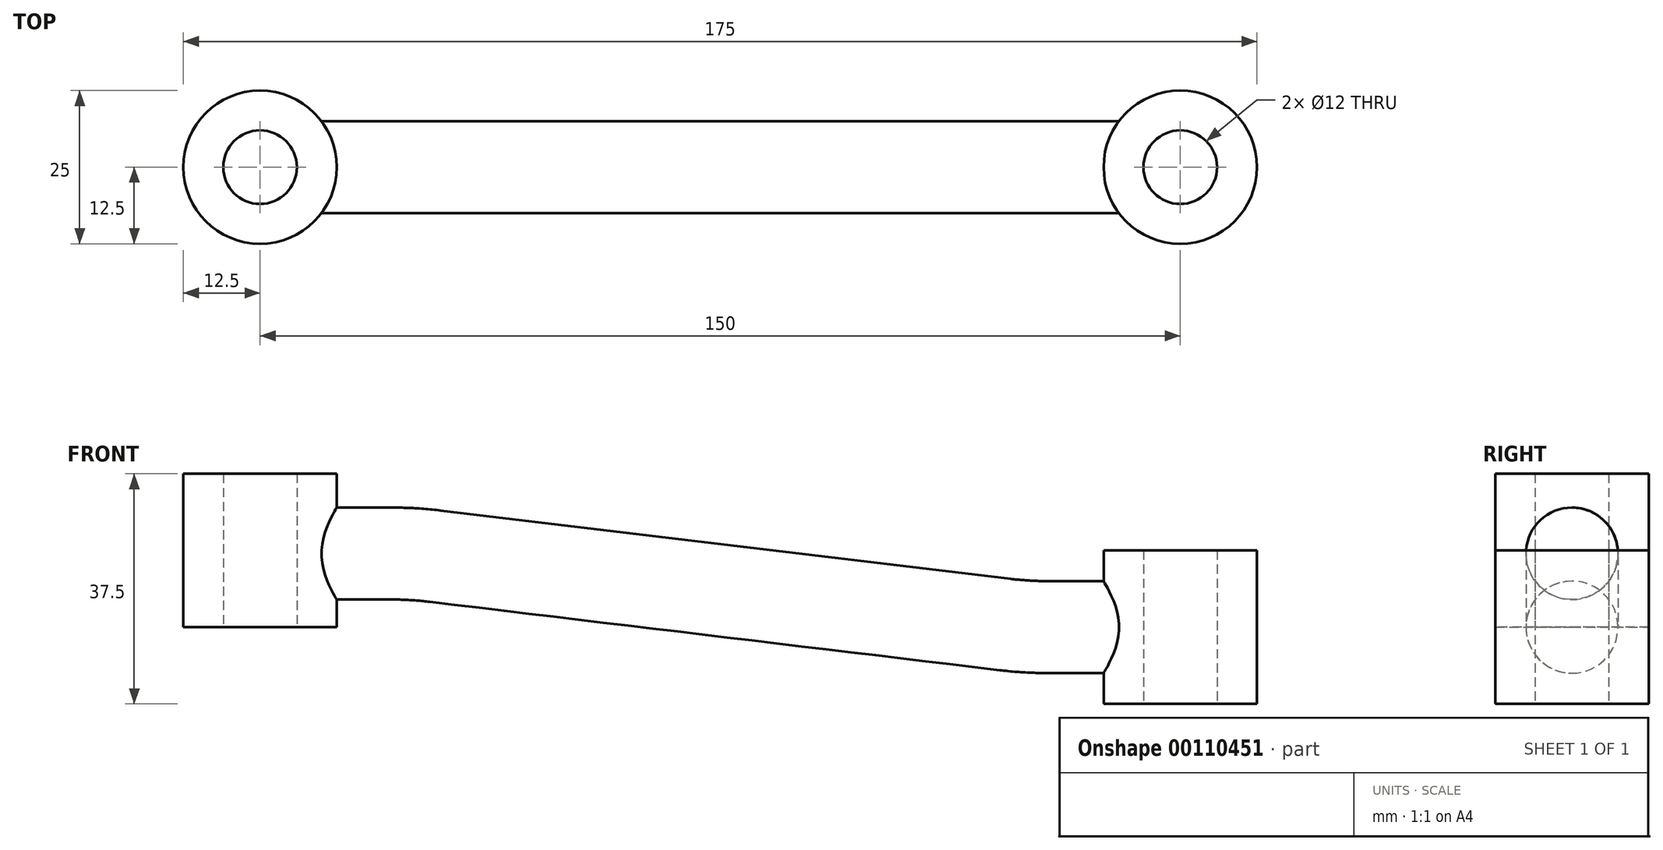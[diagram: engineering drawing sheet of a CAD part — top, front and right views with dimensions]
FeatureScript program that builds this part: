
annotation { "Feature Type Name" : "Feature", "Feature Type Description" : "" }
export const myFeature = defineFeature(function(context is Context, id is Id, definition is map)
    precondition{}
    {
        {
            var Q0;
            Q0=qCreatedBy(makeId("Top.planeOp"),FACE);
            var sketch = newSketch(context, id + "F0", { "sketchPlane" : qUnion([Q0])});
            skCircle(sketch, "E0", {"center": v(0, 0) * mm, "radius": 12.5 * mm});
            skCircle(sketch, "E1", {"center": v(0, 0) * mm, "radius": 6 * mm});
            skSolve(sketch);
        }
        {
            var Q0;
            Q0 = qSketchRegion(id + "F0", true);
            extrude(context, id + "F1", {"entities" : qUnion([Q0]), "depth" : 25 * mm});
        }
        {
            var Q0;
            Q0=qCreatedBy(makeId("Front.planeOp"),FACE);
            var sketch = newSketch(context, id + "F2", { "sketchPlane" : qUnion([Q0])});
            skLineSegment(sketch, "E2", {"start": v(0, 0) * mm, "end": v(0, 12) * mm, "construction": true});
            skLineSegment(sketch, "E3", {"start": v(0, 12) * mm, "end": v(21.41, 12) * mm});
            skLineSegment(sketch, "E4", {"start": v(28.56, 11.57) * mm, "end": v(121.44, 0.43) * mm});
            skLineSegment(sketch, "E5", {"start": v(128.59, 0) * mm, "end": v(150, 0) * mm});
            skPoint(sketch, "E6.visualSharp", {"position": v(25, 12) * mm});
            skArc(sketch, "E6.filletArc", {"start": v(28.56, 11.57) * mm, "mid": v(25, 11.9) * mm, "end": v(21.41, 12) * mm});
            skPoint(sketch, "E7.visualSharp", {"position": v(125, 0) * mm});
            skArc(sketch, "E7.filletArc", {"start": v(121.44, 0.43) * mm, "mid": v(125, 0.1) * mm, "end": v(128.59, 0) * mm});
            skSolve(sketch);
        }
        {
            var Q0;
            Q0=qCreatedBy(makeId("Top.planeOp"),FACE);
            var sketch = newSketch(context, id + "F3", { "sketchPlane" : qUnion([Q0])});
            skCircle(sketch, "E8", {"center": v(150, 0) * mm, "radius": 6 * mm});
            skCircle(sketch, "E9", {"center": v(150, 0) * mm, "radius": 12.5 * mm});
            skSolve(sketch);
        }
        {
            var Q0;
            Q0 = qSketchRegion(id + "F3", true);
            extrude(context, id + "F4", {"entities" : qUnion([Q0]), "endBound" : BoundingType.SYMMETRIC, "depth" : 25 * mm});
        }
        {
            var Q0;
            Q0=qCreatedBy(makeId("Right.planeOp"),FACE);
            var sketch = newSketch(context, id + "F5", { "sketchPlane" : qUnion([Q0])});
            skLineSegment(sketch, "E10", {"start": v(0, 0) * mm, "end": v(0, 12) * mm, "construction": true});
            skCircle(sketch, "E11", {"center": v(0, 12) * mm, "radius": 7.5 * mm});
            skSolve(sketch);
        }
        {
            var Q0;
            Q0 = qSketchRegion(id + "F5", true);
            var Q1;
            Q1=sQuery(id+"F2.wireOp",EDGE,"E3");
            var Q2;
            Q2=sQuery(id+"F2.wireOp",EDGE,"E6.filletArc");
            var Q3;
            Q3=sQuery(id+"F2.wireOp",EDGE,"E4");
            var Q4;
            Q4=sQuery(id+"F2.wireOp",EDGE,"E7.filletArc");
            var Q5;
            Q5=sQuery(id+"F2.wireOp",EDGE,"E5");
            sweep(context, id + "F6", {"operationType" : NewBodyOperationType.ADD, "profiles" : qUnion([Q0]), "path" : qUnion([Q1, Q2, Q3, Q4, Q5])});
        }
        {
            var Q0;
            Q0=qCreatedBy(makeId("Top.planeOp"),FACE);
            var sketch = newSketch(context, id + "F7", { "sketchPlane" : qUnion([Q0])});
            skCircle(sketch, "E12", {"center": v(0, 0) * mm, "radius": 6 * mm});
            skLineSegment(sketch, "E13", {"start": v(0, 0) * mm, "end": v(150, 0) * mm, "construction": true});
            skCircle(sketch, "E14", {"center": v(150, 0) * mm, "radius": 6 * mm});
            skSolve(sketch);
        }
        {
            var Q0;
            Q0 = qSketchRegion(id + "F7", true);
            extrude(context, id + "F8", {"entities" : qUnion([Q0]), "operationType" : NewBodyOperationType.REMOVE, "endBound" : BoundingType.SYMMETRIC, "oppositeDirection" : true, "depth" : 50 * mm});
        }
    });
